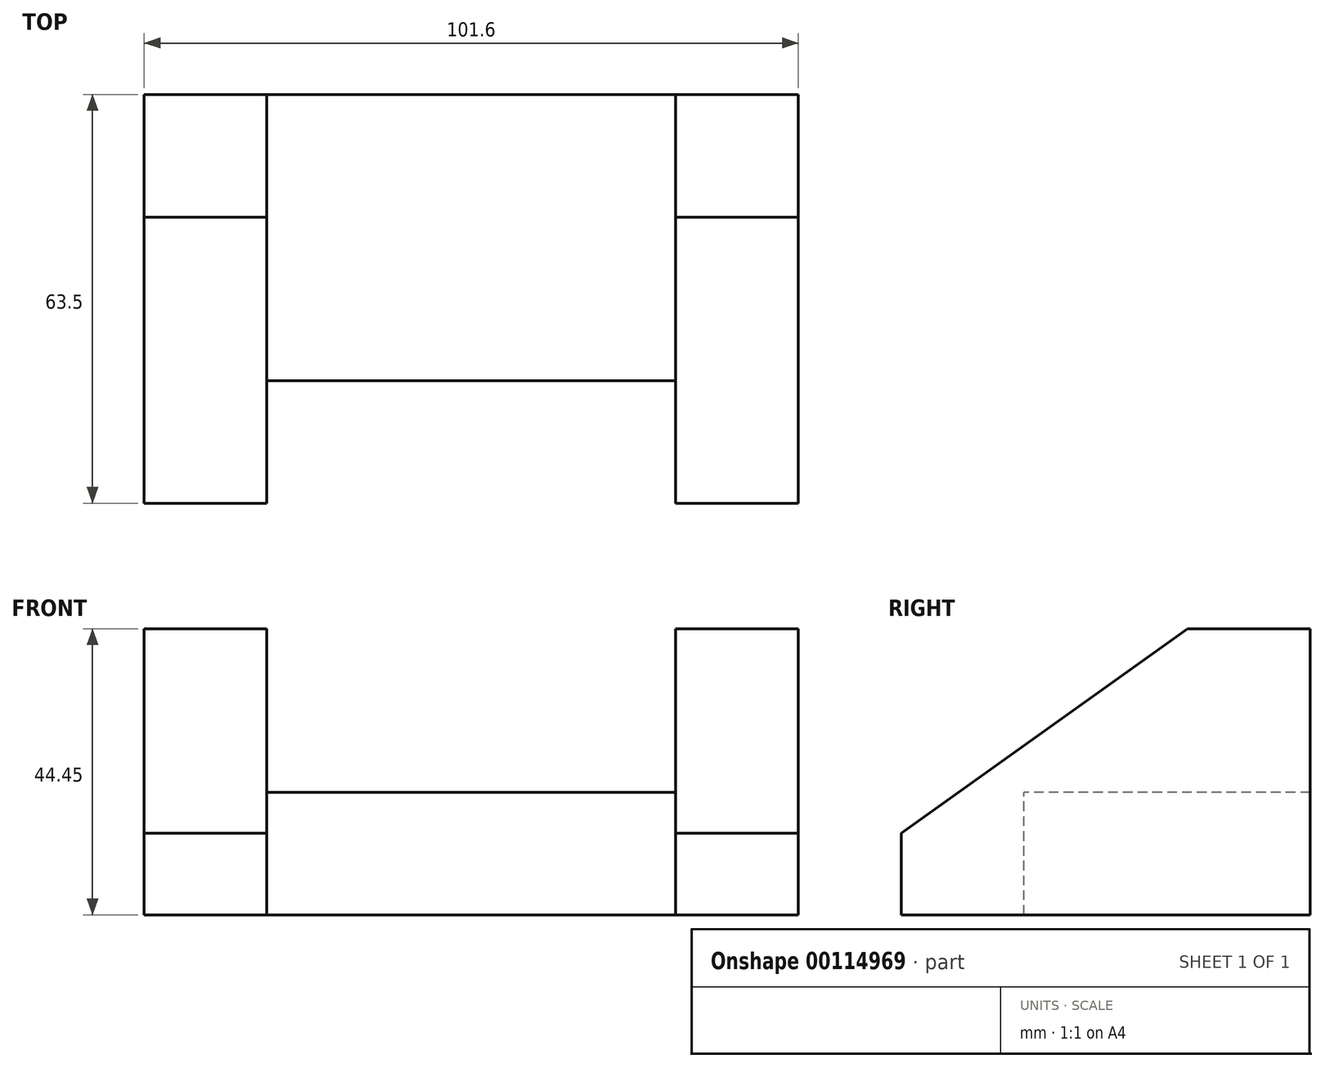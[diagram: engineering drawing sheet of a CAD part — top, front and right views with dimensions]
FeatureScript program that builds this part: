
annotation { "Feature Type Name" : "Feature", "Feature Type Description" : "" }
export const myFeature = defineFeature(function(context is Context, id is Id, definition is map)
    precondition{}
    {
        {
            var Q0;
            Q0=qCreatedBy(makeId("Top.planeOp"),FACE);
            var sketch = newSketch(context, id + "F0", { "sketchPlane" : qUnion([Q0])});
            skLineSegment(sketch, "E0.bottom", {"start": v(-27.44, 20.09) * mm, "end": v(36.06, 20.09) * mm});
            skLineSegment(sketch, "E0.top", {"start": v(-27.44, -24.36) * mm, "end": v(36.06, -24.36) * mm});
            skLineSegment(sketch, "E0.left", {"start": v(-27.44, 20.09) * mm, "end": v(-27.44, -24.36) * mm});
            skLineSegment(sketch, "E0.right", {"start": v(36.06, 20.09) * mm, "end": v(36.06, -24.36) * mm});
            skSolve(sketch);
        }
        {
            var Q0;
            Q0=makeQuery(id+"F0.imprint","IMPRINT",FACE,{"disambiguationData":[TD([[makeQuery(id+"F0.imprint","IMPRINT",EDGE,{"derivedFrom":sQuery(id+"F0.wireOp",EDGE,"E0.bottom")}),-1.0]])]});
            extrude(context, id + "F1", {"entities" : qUnion([Q0]), "depth" : 19.05 * mm});
        }
        {
            var Q0;
            Q0=qCreatedBy(makeId("Right.planeOp"),FACE);
            cPlane(context, id + "F2", {"entities" : qUnion([Q0]), "cplaneType" : CPlaneType.OFFSET, "offset" : 36.07 * mm, "width" : 152.4 * mm, "height" : 152.4 * mm});
        }
        {
            var Q0;
            Q0=qCreatedBy(id+"F2.planeOp",FACE);
            var sketch = newSketch(context, id + "F3", { "sketchPlane" : qUnion([Q0])});
            skLineSegment(sketch, "E1", {"start": v(20.09, 0) * mm, "end": v(-43.41, 0) * mm});
            skLineSegment(sketch, "E2", {"start": v(20.09, 0) * mm, "end": v(20.09, 44.45) * mm});
            skLineSegment(sketch, "E3", {"start": v(20.09, 44.45) * mm, "end": v(1.04, 44.45) * mm});
            skLineSegment(sketch, "E4", {"start": v(-43.41, 0) * mm, "end": v(-43.41, 12.7) * mm});
            skLineSegment(sketch, "E5", {"start": v(-43.41, 12.7) * mm, "end": v(1.04, 44.45) * mm});
            skSolve(sketch);
        }
        {
            var Q0;
            Q0=qCreatedBy(id+"F2.planeOp",FACE);
            cPlane(context, id + "F4", {"entities" : qUnion([Q0]), "cplaneType" : CPlaneType.OFFSET, "offset" : 31.75 * mm, "oppositeDirection" : true, "width" : 152.4 * mm, "height" : 152.4 * mm});
        }
        {
            var Q0;
            Q0=makeQuery(id+"F3.imprint","IMPRINT",FACE,{"disambiguationData":[TD([[makeQuery(id+"F3.imprint","IMPRINT",EDGE,{"derivedFrom":sQuery(id+"F3.wireOp",EDGE,"E1")}),-1.0]])]});
            extrude(context, id + "F5", {"entities" : qUnion([Q0]), "depth" : 19.05 * mm});
        }
        {
            var Q0;
            Q0=makeQuery(id+"F5.opExtrude","SWEPT_BODY",BODY,{"disambiguationData":[OSD([sQuery(id+"F3.wireOp",EDGE,"E1"),sQuery(id+"F3.wireOp",EDGE,"E2"),sQuery(id+"F3.wireOp",EDGE,"E3"),sQuery(id+"F3.wireOp",EDGE,"E4"),sQuery(id+"F3.wireOp",EDGE,"E5")])]});
            var Q1;
            Q1=qCreatedBy(id+"F4.planeOp",FACE);
            mirror(context, id + "F6", {"operationType" : NewBodyOperationType.ADD, "entities" : qUnion([Q0]), "mirrorPlane" : qUnion([Q1])});
        }
    });
